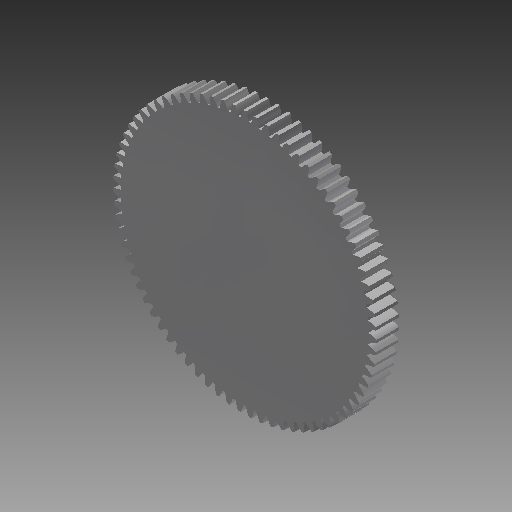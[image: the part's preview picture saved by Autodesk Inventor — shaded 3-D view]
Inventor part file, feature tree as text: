
AUTODESK INVENTOR PART (.ipt)
format: ipt  version: 2019 (Build 230136000, 136)  size: 450,560 bytes
history: native  units: mm (DEFAULTED — no unit token found)
features: plane x3, other x3, sketch x2, extrude x1
ambient origin geometry x8: Origin, YZ Plane, XZ Plane, XY Plane, X Axis, Y Axis, Z Axis, Center Point
bodies: Solid1 (feature_tree)
feature tree (9):
  extrude  "Extrusion1"  Depth=20.0mm TaperAngle=0.0deg
  plane  "Work Plane2"
  plane  "Work Plane8"
  plane  "Work Plane9"
  other  "Spur Gear"
  sketch  "Sketch1"  dims[d0=231.499195mm d1=20.0mm d2=0.0mm]
  sketch  "Sketch2"  dims[d3=225.503356mm d4=10.0mm d5=0.0mm d16=224.0mm d17=0.0mm d34=0.418879mm d39=0.0mm d41=0.0mm d43=224.0mm d46=224.0mm d47=0.0mm d48=0.0mm]
  other  "Srf1"
  other  "Pitch Diameter"
